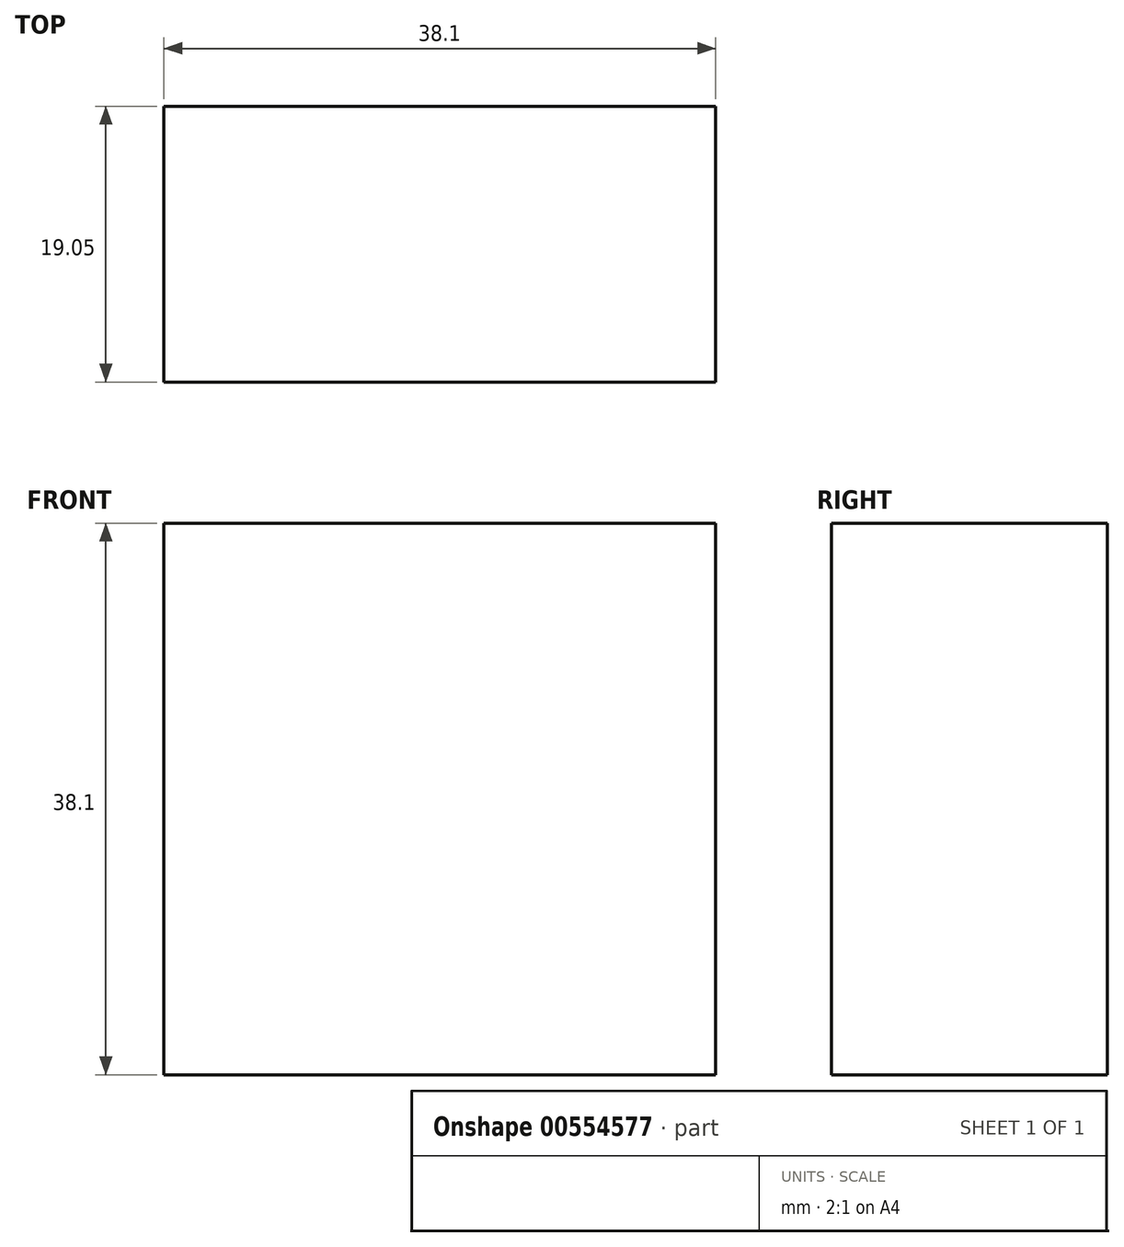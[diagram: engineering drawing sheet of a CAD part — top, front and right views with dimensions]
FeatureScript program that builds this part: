
annotation { "Feature Type Name" : "Feature", "Feature Type Description" : "" }
export const myFeature = defineFeature(function(context is Context, id is Id, definition is map)
    precondition{}
    {
        {
            var Q0;
            Q0=qCreatedBy(makeId("Front.planeOp"),FACE);
            var sketch = newSketch(context, id + "F0", { "sketchPlane" : qUnion([Q0])});
            skLineSegment(sketch, "E0", {"start": v(-22.37, 18.49) * mm, "end": v(15.73, 18.49) * mm});
            skLineSegment(sketch, "E1", {"start": v(15.73, 18.49) * mm, "end": v(15.73, -19.61) * mm});
            skLineSegment(sketch, "E2", {"start": v(15.73, -19.61) * mm, "end": v(-22.37, -19.61) * mm});
            skLineSegment(sketch, "E3", {"start": v(-22.37, -19.61) * mm, "end": v(-22.37, 18.49) * mm});
            skSolve(sketch);
        }
        {
            var Q0;
            Q0 = qSketchRegion(id + "F0", true);
            extrude(context, id + "F1", {"entities" : qUnion([Q0]), "depth" : 19.05 * mm, "offsetDistance" : 25.4 * mm});
        }
    });
